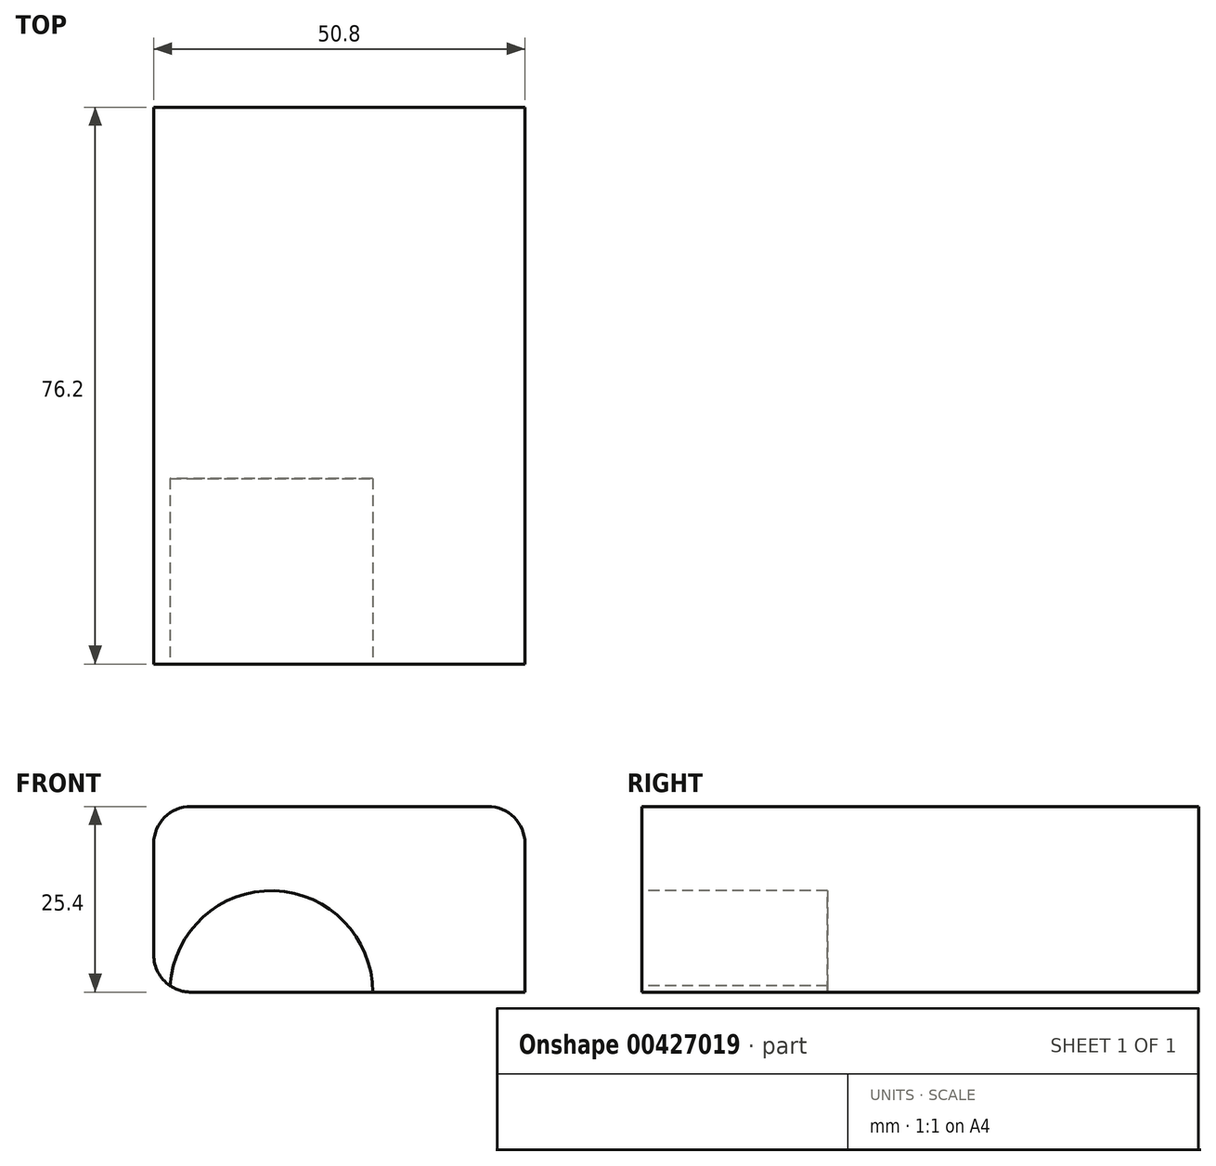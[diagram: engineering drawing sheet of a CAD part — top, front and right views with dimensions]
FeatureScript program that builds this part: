
annotation { "Feature Type Name" : "Feature", "Feature Type Description" : "" }
export const myFeature = defineFeature(function(context is Context, id is Id, definition is map)
    precondition{}
    {
        {
            var Q0;
            Q0=qCreatedBy(makeId("Top.planeOp"),FACE);
            var sketch = newSketch(context, id + "F0", { "sketchPlane" : qUnion([Q0])});
            skLineSegment(sketch, "E0.bottom", {"start": v(-50.8, -18.75) * mm, "end": v(0, -18.75) * mm});
            skLineSegment(sketch, "E0.top", {"start": v(-50.8, 0) * mm, "end": v(0, 0) * mm});
            skLineSegment(sketch, "E0.left", {"start": v(-50.8, -18.75) * mm, "end": v(-50.8, 0) * mm});
            skLineSegment(sketch, "E0.right", {"start": v(0, -18.75) * mm, "end": v(0, 0) * mm});
            skSolve(sketch);
        }
        {
            var Q0;
            Q0=sQuery(id+"F0.wireOp",EDGE,"E0.top");
            extrude(context, id + "F1", {"bodyType" : ToolBodyType.SURFACE, "surfaceEntities" : qUnion([Q0]), "depth" : 25.4 * mm});
        }
        {
            var Q0;
            Q0=makeQuery(id+"F1.opExtrude","SWEPT_FACE",FACE,{"disambiguationData":[OSD([sQuery(id+"F0.wireOp",EDGE,"E0.top")])]});
            extrude(context, id + "F2", {"entities" : qUnion([Q0]), "depth" : 76.2 * mm});
        }
        {
            var Q0;
            {var subQ0=sQuery(id+"F0.wireOp",VERTEX,"E0.top.start");Q0=makeQuery(id+"F2.opExtrude","SWEPT_EDGE",EDGE,{"disambiguationData":[OSD([subQ0]),TDD([makeQuery(id+"F1.opExtrude","CAP_VERTEX",VERTEX,{"disambiguationData":[OSD([subQ0])],"isStart":false})])]});}
            var Q1;
            {var subQ0=sQuery(id+"F0.wireOp",VERTEX,"E0.top.start");Q1=makeQuery(id+"F2.opExtrude","SWEPT_EDGE",EDGE,{"disambiguationData":[OSD([subQ0]),TDD([makeQuery(id+"F1.opExtrude","CAP_VERTEX",VERTEX,{"disambiguationData":[OSD([subQ0])],"isStart":true})])]});}
            var Q2;
            {var subQ0=sQuery(id+"F0.wireOp",VERTEX,"E0.top.end");Q2=makeQuery(id+"F2.opExtrude","SWEPT_EDGE",EDGE,{"disambiguationData":[OSD([subQ0]),TDD([makeQuery(id+"F1.opExtrude","CAP_VERTEX",VERTEX,{"disambiguationData":[OSD([subQ0])],"isStart":false})])]});}
            fillet(context, id + "F3", {"entities" : qUnion([Q0, Q1, Q2]), "radius" : 5.08 * mm, "tangentPropagation" : true, "allowEdgeOverflow" : false});
        }
        {
            var Q0;
            Q0=makeQuery(id+"F2.opExtrude","CAP_FACE",FACE,{"disambiguationData":[OSD([sQuery(id+"F0.wireOp",EDGE,"E0.top")])],"isStart":false});
            var sketch = newSketch(context, id + "F4", { "sketchPlane" : qUnion([Q0])});
            skCircle(sketch, "E1", {"center": v(-34.72, 0) * mm, "radius": 13.88 * mm});
            skSolve(sketch);
        }
        {
            var Q0;
            {var subQ0=sQuery(id+"F4.wireOp",EDGE,"E1");var subQ1=sQuery(id+"F0.wireOp",EDGE,"E0.top");var subQ5=makeQuery(id+"F2.opExtrude","CAP_EDGE",EDGE,{"disambiguationData":[OSD([subQ1]),TDD([makeQuery(id+"F1.opExtrude","CAP_EDGE",EDGE,{"disambiguationData":[OSD([subQ1])],"isStart":true})])],"isStart":false});var subQ6=makeQuery(id+"F4.imprint","INTERSECT",VERTEX,{"derivedFrom":[subQ5,subQ0]});Q0=makeQuery(id+"F4.imprint","IMPRINT",FACE,{"disambiguationData":[TD([[makeQuery(id+"F4.imprint","IMPRINT",EDGE,{"disambiguationData":[TD([[subQ6,-1.0]])],"derivedFrom":subQ0}),1.0]])]});}
            extrude(context, id + "F5", {"entities" : qUnion([Q0]), "operationType" : NewBodyOperationType.REMOVE, "oppositeDirection" : true, "depth" : 25.4 * mm});
        }
    });
